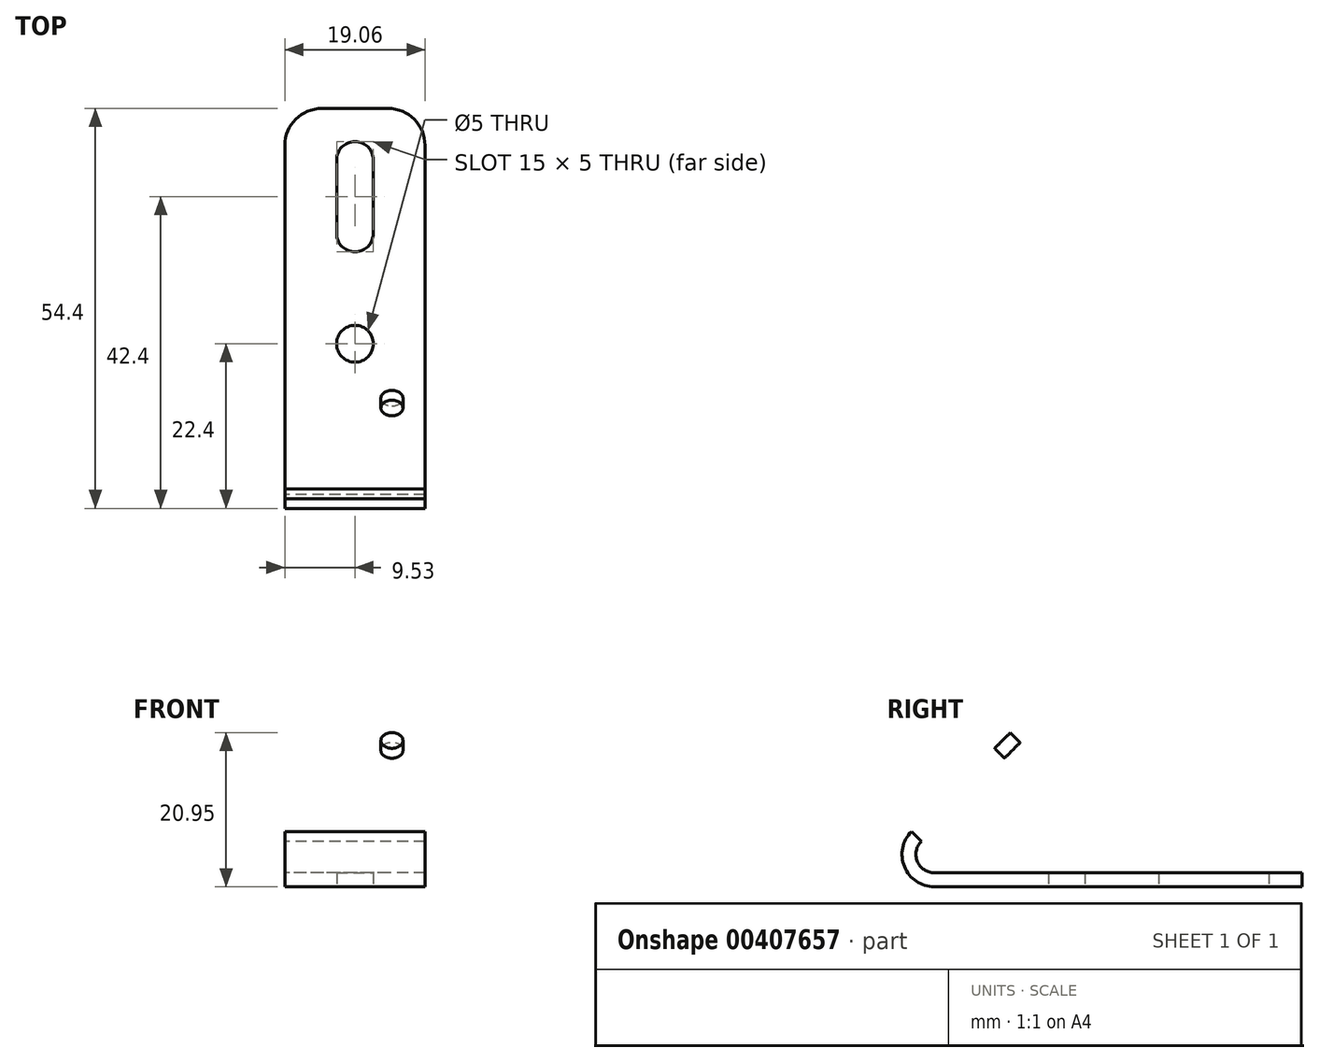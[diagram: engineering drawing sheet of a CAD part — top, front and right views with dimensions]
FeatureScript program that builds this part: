
annotation { "Feature Type Name" : "Feature", "Feature Type Description" : "" }
export const myFeature = defineFeature(function(context is Context, id is Id, definition is map)
    precondition{}
    {
        {
            var Q0;
            Q0=qCreatedBy(makeId("Right.planeOp"),FACE);
            var sketch = newSketch(context, id + "F0", { "sketchPlane" : qUnion([Q0])});
            skLineSegment(sketch, "E0", {"start": v(0, 0) * mm, "end": v(50, 0) * mm});
            skCircle(sketch, "E1", {"center": v(0, 4.4) * mm, "radius": 4.4 * mm, "construction": true});
            skLineSegment(sketch, "E2", {"start": v(-3.11, 7.51) * mm, "end": v(14.57, 25.19) * mm});
            skArc(sketch, "E3", {"start": v(0, 0) * mm, "mid": v(-4.07, 2.72) * mm, "end": v(-3.11, 7.51) * mm});
            skLineSegment(sketch, "E4.0", {"start": v(-1.77, 6.17) * mm, "end": v(15.9, 23.85) * mm});
            skArc(sketch, "E4.1", {"start": v(0, 1.9) * mm, "mid": v(-2.3, 3.44) * mm, "end": v(-1.77, 6.17) * mm});
            skLineSegment(sketch, "E4.2", {"start": v(0, 1.9) * mm, "end": v(50, 1.9) * mm});
            skLineSegment(sketch, "E5", {"start": v(15.9, 23.85) * mm, "end": v(14.57, 25.19) * mm});
            skLineSegment(sketch, "E6", {"start": v(50, 0) * mm, "end": v(50, 1.9) * mm});
            skSolve(sketch);
        }
        {
            var Q0;
            Q0=qSketchRegion(id+"F0",true);
            extrude(context, id + "F1", {"entities" : qUnion([Q0]), "endBound" : BoundingType.SYMMETRIC, "depth" : 19.05 * mm});
        }
        {
            var Q0;
            Q0=makeQuery(id+"F1.opExtrude","SWEPT_FACE",FACE,{"disambiguationData":[OSD([sQuery(id+"F0.wireOp",EDGE,"E0")])]});
            var sketch = newSketch(context, id + "F2", { "sketchPlane" : qUnion([Q0])});
            skCircle(sketch, "E7", {"center": v(0, -43) * mm, "radius": 2.5 * mm});
            skPoint(sketch, "E7.centerSnap0", {"position": v(0, -50) * mm});
            skCircle(sketch, "E8", {"center": v(0, -33) * mm, "radius": 2.5 * mm});
            skCircle(sketch, "E9", {"center": v(0, -18) * mm, "radius": 2.5 * mm});
            skLineSegment(sketch, "E10.bottom", {"start": v(-2.5, -33) * mm, "end": v(2.5, -33) * mm});
            skLineSegment(sketch, "E10.top", {"start": v(-2.5, -43) * mm, "end": v(2.5, -43) * mm});
            skLineSegment(sketch, "E10.left", {"start": v(-2.5, -33) * mm, "end": v(-2.5, -43) * mm});
            skLineSegment(sketch, "E10.right", {"start": v(2.5, -33) * mm, "end": v(2.5, -43) * mm});
            skSolve(sketch);
        }
        {
            var Q0;
            {var subQ0=sQuery(id+"F2.wireOp",EDGE,"E10.top");Q0=makeQuery(id+"F2.imprint","IMPRINT",FACE,{"disambiguationData":[TD([[makeQuery(id+"F2.imprint","IMPRINT",EDGE,{"derivedFrom":subQ0}),-1.0]])]});}
            var Q1;
            {var subQ0=sQuery(id+"F2.wireOp",EDGE,"E10.top");Q1=makeQuery(id+"F2.imprint","IMPRINT",FACE,{"disambiguationData":[TD([[makeQuery(id+"F2.imprint","IMPRINT",EDGE,{"derivedFrom":subQ0}),1.0]])]});}
            var Q2;
            {var subQ0=sQuery(id+"F2.wireOp",EDGE,"E10.left");Q2=makeQuery(id+"F2.imprint","IMPRINT",FACE,{"disambiguationData":[TD([[makeQuery(id+"F2.imprint","IMPRINT",EDGE,{"derivedFrom":subQ0}),1.0]])]});}
            var Q3;
            {var subQ0=sQuery(id+"F2.wireOp",EDGE,"E10.bottom");Q3=makeQuery(id+"F2.imprint","IMPRINT",FACE,{"disambiguationData":[TD([[makeQuery(id+"F2.imprint","IMPRINT",EDGE,{"derivedFrom":subQ0}),1.0]])]});}
            var Q4;
            {var subQ0=sQuery(id+"F2.wireOp",EDGE,"E10.bottom");Q4=makeQuery(id+"F2.imprint","IMPRINT",FACE,{"disambiguationData":[TD([[makeQuery(id+"F2.imprint","IMPRINT",EDGE,{"derivedFrom":subQ0}),-1.0]])]});}
            var Q5;
            Q5=makeQuery(id+"F2.imprint","IMPRINT",FACE,{"disambiguationData":[TD([[makeQuery(id+"F2.imprint","IMPRINT",EDGE,{"derivedFrom":sQuery(id+"F2.wireOp",EDGE,"E9")}),1.0]])]});
            var Q6;
            Q6=makeQuery(id+"F1.opExtrude","SWEPT_FACE",FACE,{"disambiguationData":[OSD([sQuery(id+"F0.wireOp",EDGE,"E4.2")])]});
            extrude(context, id + "F3", {"entities" : qUnion([Q0, Q1, Q2, Q3, Q4, Q5]), "operationType" : NewBodyOperationType.REMOVE, "endBound" : BoundingType.UP_TO_SURFACE, "oppositeDirection" : true, "endBoundEntityFace" : qUnion([Q6]), "depth" : 25.4 * mm});
        }
        {
            var Q0;
            Q0=makeQuery(id+"F1.opExtrude","SWEPT_FACE",FACE,{"disambiguationData":[OSD([sQuery(id+"F0.wireOp",EDGE,"E2")])]});
            var sketch = newSketch(context, id + "F4", { "sketchPlane" : qUnion([Q0])});
            skLineSegment(sketch, "E11", {"start": v(0, 28.11) * mm, "end": v(0, 3.11) * mm, "construction": true});
            skCircle(sketch, "E12", {"center": v(-5.03, 20.61) * mm, "radius": 1.5 * mm});
            skCircle(sketch, "E13.MirrorC", {"center": v(5.03, 20.61) * mm, "radius": 1.5 * mm});
            skSolve(sketch);
        }
        {
            var Q0;
            Q0=makeQuery(id+"F4.imprint","IMPRINT",FACE,{"disambiguationData":[TD([[makeQuery(id+"F4.imprint","IMPRINT",EDGE,{"derivedFrom":sQuery(id+"F4.wireOp",EDGE,"E12")}),1.0]])]});
            var Q1;
            Q1=makeQuery(id+"F4.imprint","IMPRINT",FACE,{"disambiguationData":[TD([[makeQuery(id+"F4.imprint","IMPRINT",EDGE,{"derivedFrom":sQuery(id+"F4.wireOp",EDGE,"E13.MirrorC")}),-1.0]])]});
            var Q2;
            Q2=makeQuery(id+"F1.opExtrude","SWEPT_FACE",FACE,{"disambiguationData":[OSD([sQuery(id+"F0.wireOp",EDGE,"E4.0")])]});
            extrude(context, id + "F5", {"entities" : qUnion([Q0, Q1]), "operationType" : NewBodyOperationType.REMOVE, "endBound" : BoundingType.UP_TO_SURFACE, "oppositeDirection" : true, "endBoundEntityFace" : qUnion([Q2]), "depth" : 25.4 * mm});
        }
        {
            var Q0;
            Q0=makeQuery(id+"F1.opExtrude","CAP_EDGE",EDGE,{"disambiguationData":[OSD([sQuery(id+"F0.wireOp",EDGE,"E5")])],"isStart":false});
            var Q1;
            Q1=makeQuery(id+"F1.opExtrude","CAP_EDGE",EDGE,{"disambiguationData":[OSD([sQuery(id+"F0.wireOp",EDGE,"E5")])],"isStart":true});
            var Q2;
            Q2=makeQuery(id+"F1.opExtrude","CAP_EDGE",EDGE,{"disambiguationData":[OSD([sQuery(id+"F0.wireOp",EDGE,"E6")])],"isStart":false});
            var Q3;
            Q3=makeQuery(id+"F1.opExtrude","CAP_EDGE",EDGE,{"disambiguationData":[OSD([sQuery(id+"F0.wireOp",EDGE,"E6")])],"isStart":true});
            fillet(context, id + "F6", {"entities" : qUnion([Q0, Q1, Q2, Q3]), "radius" : 5 * mm, "tangentPropagation" : true, "allowEdgeOverflow" : false});
        }
    });
